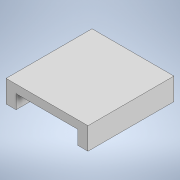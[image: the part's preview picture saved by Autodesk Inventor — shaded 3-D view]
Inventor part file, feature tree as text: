
AUTODESK INVENTOR PART (.ipt)
format: ipt  version: 2022 (Build 260153000, 153)  size: 181,248 bytes
history: native  units: in
note: dims shown in document units (in); Inventor stores cm internally (conversion verified against a paired STEP export)
features: sketch x6, extrude x5, other x2, plane x1
ambient origin geometry x8: Origin, YZ Plane, XZ Plane, XY Plane, X Axis, Y Axis, Z Axis, Center Point
bodies: Solid1 (feature_tree)
feature tree (14):
  other  "ExpansionCard"
  sketch  "Sketch1"  dims[d0=35.0in d1=5.0in]
  sketch  "Sketch2"  dims[d2=8.0in d3=39.9566in]
  plane  "Work Plane1"
  sketch  "Sketch3"  dims[d4=31.9566in d5=8.5in]
  extrude  "Extrusion2"  Depth=5.0in
  extrude  "Extrusion3"  Depth=39.9566in
  extrude  "Extrusion4"  Depth=8.5in
  extrude  "Extrusion5"  Depth=2.0in
  extrude  "Extrusion6"  Depth=6.8in TaperAngle=0.0deg
  sketch  "Sketch4"  dims[d6=2.7in d9=2.0in]
  sketch  "Sketch5"  dims[d10=4.0in d11=0.0in d12=6.8in d13=0.0in]
  sketch  "Sketch6"  dims[d14=8.0in d15=0.0in d16=0.1in d17=0.0in d18=0.1in d19=0.0in]
  other  "MeshFeature1"
